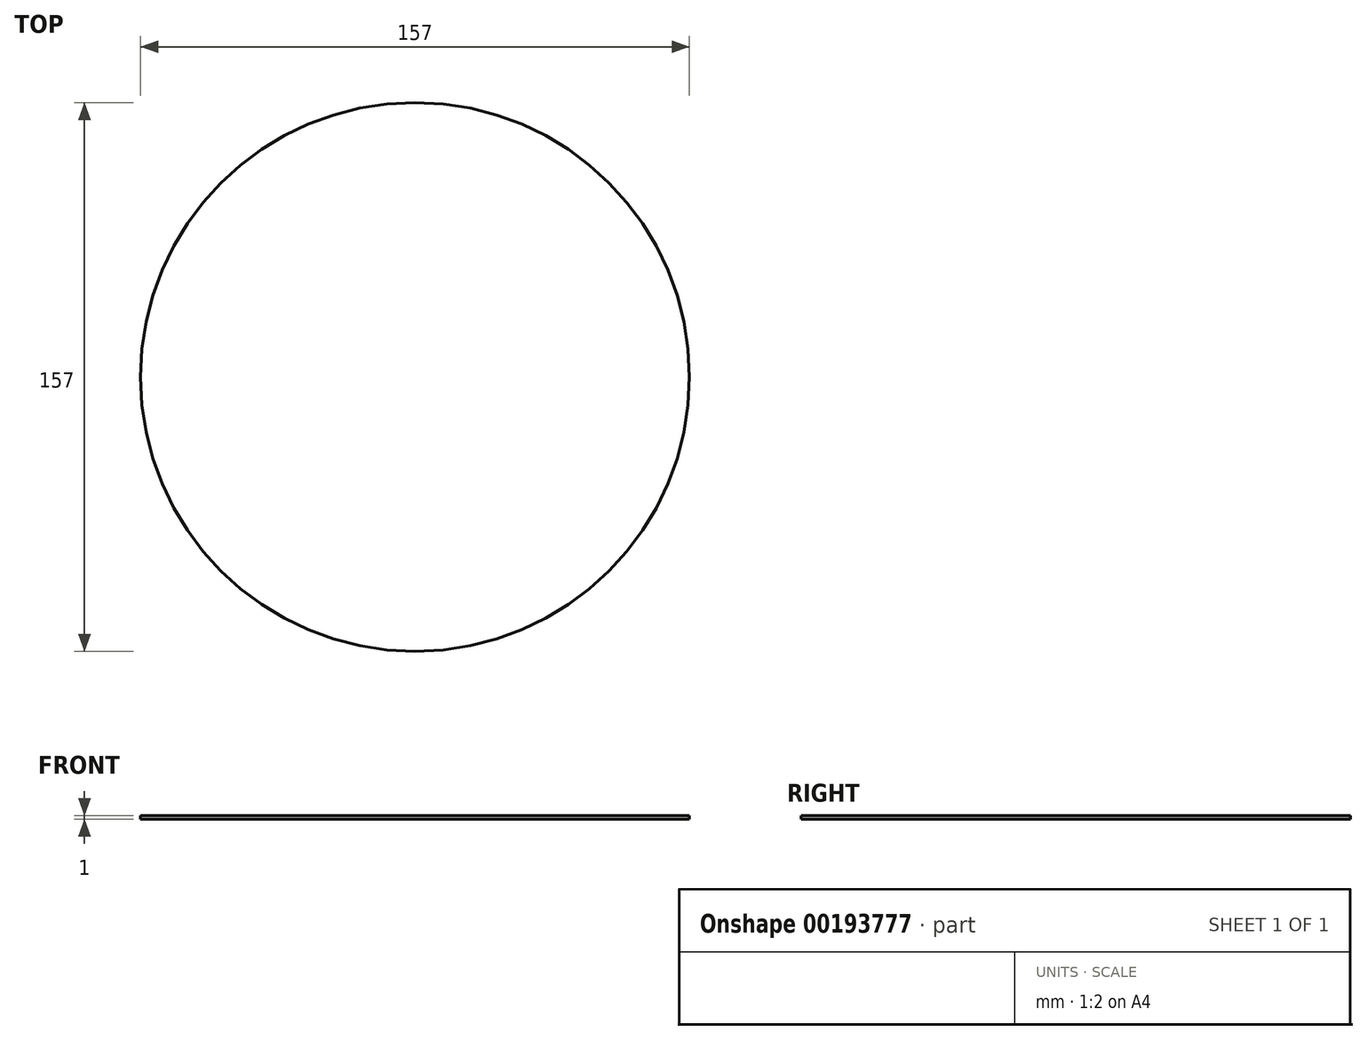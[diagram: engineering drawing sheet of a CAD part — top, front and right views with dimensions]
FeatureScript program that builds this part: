
annotation { "Feature Type Name" : "Feature", "Feature Type Description" : "" }
export const myFeature = defineFeature(function(context is Context, id is Id, definition is map)
    precondition{}
    {
        {
            var Q0;
            Q0=qCreatedBy(makeId("Top.planeOp"),FACE);
            var sketch = newSketch(context, id + "F0", { "sketchPlane" : qUnion([Q0])});
            skCircle(sketch, "E0", {"center": v(0.01, -6.82) * mm, "radius": 78.5 * mm});
            skSolve(sketch);
        }
        {
            var Q0;
            Q0=makeQuery(id+"F0.imprint","IMPRINT",FACE,{"disambiguationData":[TD([[makeQuery(id+"F0.imprint","IMPRINT",EDGE,{"derivedFrom":sQuery(id+"F0.wireOp",EDGE,"E0")}),1.0]])]});
            extrude(context, id + "F1", {"entities" : qUnion([Q0]), "depth" : 1 * mm});
        }
    });
